# Revit family: Gorter RV 800x800mm
name_source: partatom
category: Generic Models
units: mm (PartAtom-declared; Revit-internal decimal feet)

## family parameters
Can host rebar = No
Cut with Voids When Loaded = Yes
Host = Face
Part Type = Normal
Room Calculation Point = No
Round Connector Dimension = Use Diameter
Shared = Yes

## types (5) — shared parameters
Manufacturer = Gorter
Model = RV
belasting = 15 kN
binnenluik = tbv betonvulling
brandwerend 90 min = nee
gasdrukveer = nee
geïsoleerd = nee
materiaal = bcb_staal
rubberen_afdichting = enkel
scharnierend = nee
sluiting = 4
vergrendeling = nee
vullen_met_beton = ja
zero-valued in all types: Default Elevation

## per-type parameters (varying)
| type | Description | binnenmaat_breedte | binnenmaat_lengte | gewicht | uitwendige_breedte | uitwendige_lengte |
| RV 600x400mm | RV 64 | 600 mm  [stored 1.9685 ft] | 400 mm  [stored 1.31234 ft] | 22 | 705 mm  [stored 2.31299 ft] | 505 mm  [stored 1.65682 ft] |
| RV 600x600mm | RV 66 | 600 mm  [stored 1.9685 ft] | 600 mm  [stored 1.9685 ft] | 29 | 705 mm  [stored 2.31299 ft] | 705 mm  [stored 2.31299 ft] |
| RV 800x600mm | RV 86 | 800 mm  [stored 2.62467 ft] | 600 mm  [stored 1.9685 ft] | 37 | 905 mm  [stored 2.96916 ft] | 705 mm  [stored 2.31299 ft] |
| RV 800x800mm | RV 88 | 800 mm  [stored 2.62467 ft] | 800 mm  [stored 2.62467 ft] | 45 | 905 mm  [stored 2.96916 ft] | 905 mm  [stored 2.96916 ft] |
| RV 1000x1000mm | RV 110 | 1000 mm  [stored 3.28084 ft] | 1000 mm  [stored 3.28084 ft] | 45 | 1105 mm  [stored 3.62533 ft] | 1105 mm  [stored 3.62533 ft] |

note: [stored X ft] marks values corroborated as IEEE doubles in the binary element streams (Revit-internal decimal feet)

## geometry (parser evidence)
native form markers: Blend x4, Sweep x4
no freeform markers — native parametric forms only
